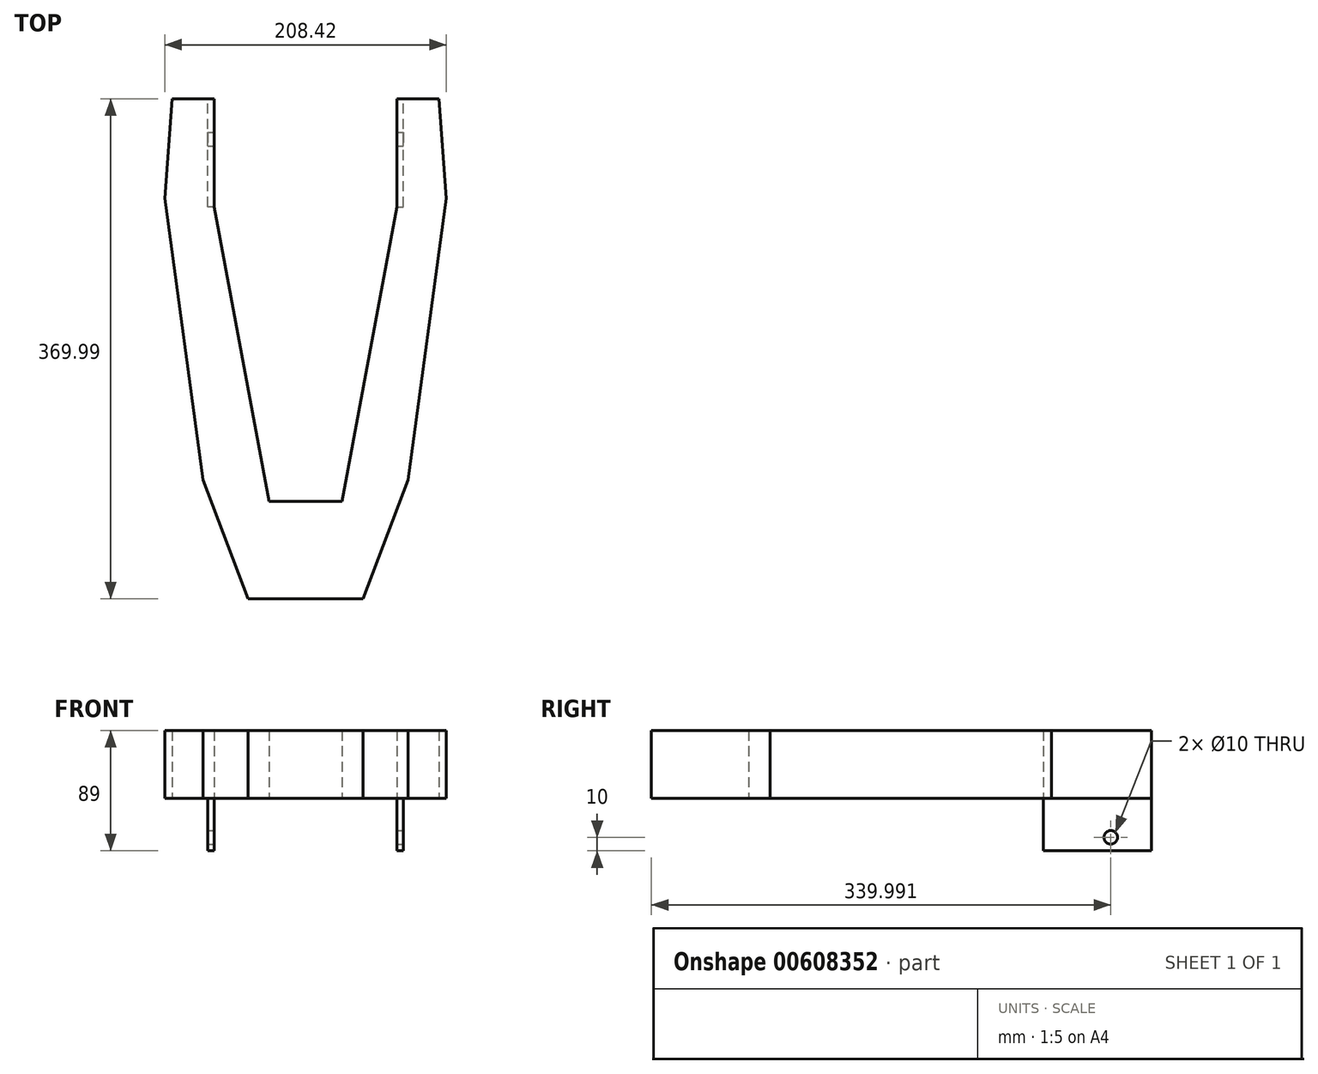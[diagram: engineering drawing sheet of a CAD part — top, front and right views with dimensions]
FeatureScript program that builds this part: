
annotation { "Feature Type Name" : "Feature", "Feature Type Description" : "" }
export const myFeature = defineFeature(function(context is Context, id is Id, definition is map)
    precondition{}
    {
        {
            var Q0;
            Q0=qCreatedBy(makeId("Top.planeOp"),FACE);
            var sketch = newSketch(context, id + "F0", { "sketchPlane" : qUnion([Q0])});
            skLineSegment(sketch, "E0", {"start": v(0, -141.26) * mm, "end": v(42.57, -141.26) * mm});
            skLineSegment(sketch, "E1", {"start": v(42.57, -141.26) * mm, "end": v(75.94, -53.33) * mm});
            skLineSegment(sketch, "E2", {"start": v(75.94, -53.33) * mm, "end": v(104.2, 154.89) * mm});
            skLineSegment(sketch, "E3", {"start": v(104.2, 154.89) * mm, "end": v(98.82, 228.73) * mm});
            skLineSegment(sketch, "E4", {"start": v(98.82, 228.73) * mm, "end": v(67.5, 228.73) * mm});
            skLineSegment(sketch, "E5", {"start": v(67.5, 228.73) * mm, "end": v(67.5, 148.73) * mm});
            skLineSegment(sketch, "E6", {"start": v(67.5, 148.73) * mm, "end": v(27, -69.27) * mm});
            skLineSegment(sketch, "E7", {"start": v(27, -69.27) * mm, "end": v(0, -69.27) * mm});
            skLineSegment(sketch, "E8.MirrorCS", {"start": v(-27, -69.27) * mm, "end": v(0, -69.27) * mm});
            skLineSegment(sketch, "E9.MirrorCS", {"start": v(-67.5, 148.73) * mm, "end": v(-27, -69.27) * mm});
            skLineSegment(sketch, "E10.MirrorCS", {"start": v(-67.5, 228.73) * mm, "end": v(-67.5, 148.73) * mm});
            skLineSegment(sketch, "E11.MirrorCS", {"start": v(-98.82, 228.73) * mm, "end": v(-67.5, 228.73) * mm});
            skLineSegment(sketch, "E12.MirrorCS", {"start": v(-104.2, 154.89) * mm, "end": v(-98.82, 228.73) * mm});
            skLineSegment(sketch, "E13.MirrorCS", {"start": v(-75.94, -53.33) * mm, "end": v(-104.2, 154.89) * mm});
            skLineSegment(sketch, "E14.MirrorCS", {"start": v(-42.57, -141.26) * mm, "end": v(-75.94, -53.33) * mm});
            skLineSegment(sketch, "E15.MirrorCS", {"start": v(0, -141.26) * mm, "end": v(-42.57, -141.26) * mm});
            skLineSegment(sketch, "E16", {"start": v(-67.5, 148.73) * mm, "end": v(-72.5, 148.73) * mm});
            skLineSegment(sketch, "E17", {"start": v(-72.5, 148.73) * mm, "end": v(-72.5, 228.73) * mm});
            skLineSegment(sketch, "E18.MirrorCS", {"start": v(67.5, 148.73) * mm, "end": v(72.5, 148.73) * mm});
            skLineSegment(sketch, "E19.MirrorCS", {"start": v(72.5, 148.73) * mm, "end": v(72.5, 228.73) * mm});
            skLineSegment(sketch, "E20", {"start": v(-67.5, 198.73) * mm, "end": v(67.5, 198.73) * mm, "construction": true});
            skLineSegment(sketch, "E21", {"start": v(-30.72, -49.27) * mm, "end": v(30.72, -49.27) * mm, "construction": true});
            skSolve(sketch);
        }
        {
            var Q0;
            Q0=makeQuery(id+"F0.imprint","IMPRINT",FACE,{"disambiguationData":[TD([[makeQuery(id+"F0.imprint","IMPRINT",EDGE,{"derivedFrom":sQuery(id+"F0.wireOp",EDGE,"E0")}),1.0]])]});
            var Q1;
            {var subQ0=sQuery(id+"F0.wireOp",EDGE,"E5");Q1=makeQuery(id+"F0.imprint","IMPRINT",FACE,{"disambiguationData":[TD([[makeQuery(id+"F0.imprint","IMPRINT",EDGE,{"derivedFrom":subQ0}),1.0]])]});}
            var Q2;
            {var subQ0=sQuery(id+"F0.wireOp",EDGE,"E10.MirrorCS");Q2=makeQuery(id+"F0.imprint","IMPRINT",FACE,{"disambiguationData":[TD([[makeQuery(id+"F0.imprint","IMPRINT",EDGE,{"derivedFrom":subQ0}),-1.0]])]});}
            extrude(context, id + "F1", {"entities" : qUnion([Q0, Q1, Q2]), "depth" : 50 * mm, "offsetDistance" : 25 * mm});
        }
        {
            var Q0;
            {var subQ0=sQuery(id+"F0.wireOp",EDGE,"E10.MirrorCS");Q0=makeQuery(id+"F0.imprint","IMPRINT",FACE,{"disambiguationData":[TD([[makeQuery(id+"F0.imprint","IMPRINT",EDGE,{"derivedFrom":subQ0}),-1.0]])]});}
            var Q1;
            {var subQ0=sQuery(id+"F0.wireOp",EDGE,"E5");Q1=makeQuery(id+"F0.imprint","IMPRINT",FACE,{"disambiguationData":[TD([[makeQuery(id+"F0.imprint","IMPRINT",EDGE,{"derivedFrom":subQ0}),1.0]])]});}
            extrude(context, id + "F2", {"entities" : qUnion([Q0, Q1]), "operationType" : NewBodyOperationType.ADD, "oppositeDirection" : true, "depth" : 39 * mm, "offsetDistance" : 25 * mm});
        }
        {
            var Q0;
            Q0=makeQuery(id+"F2.opExtrude","SWEPT_FACE",FACE,{"disambiguationData":[OSD([sQuery(id+"F0.wireOp",EDGE,"E19.MirrorCS")])]});
            var sketch = newSketch(context, id + "F3", { "sketchPlane" : qUnion([Q0])});
            skCircle(sketch, "E22", {"center": v(198.73, -29) * mm, "radius": 5 * mm});
            skSolve(sketch);
        }
        {
            var Q0;
            Q0=sQuery(id+"F3.wireOp",VERTEX,"E22.center");
            var Q1;
            Q1=makeQuery(id+"F1.opExtrude","SWEPT_BODY",BODY,{"disambiguationData":[OSD([sQuery(id+"F0.wireOp",EDGE,"E0"),sQuery(id+"F0.wireOp",EDGE,"E1"),sQuery(id+"F0.wireOp",EDGE,"E2"),sQuery(id+"F0.wireOp",EDGE,"E3"),sQuery(id+"F0.wireOp",EDGE,"E4"),sQuery(id+"F0.wireOp",EDGE,"E5"),sQuery(id+"F0.wireOp",EDGE,"E6"),sQuery(id+"F0.wireOp",EDGE,"E7"),sQuery(id+"F0.wireOp",EDGE,"E8.MirrorCS"),sQuery(id+"F0.wireOp",EDGE,"E9.MirrorCS"),sQuery(id+"F0.wireOp",EDGE,"E10.MirrorCS"),sQuery(id+"F0.wireOp",EDGE,"E11.MirrorCS"),sQuery(id+"F0.wireOp",EDGE,"E12.MirrorCS"),sQuery(id+"F0.wireOp",EDGE,"E13.MirrorCS"),sQuery(id+"F0.wireOp",EDGE,"E14.MirrorCS"),sQuery(id+"F0.wireOp",EDGE,"E15.MirrorCS")])]});
            hole(context, id + "F4", {"style" : HoleStyle.SIMPLE, "endStyle" : HoleEndStyle.THROUGH, "holeDiameter" : 10 * mm, "majorDiameter" : 5 * mm, "isTappedThrough" : true, "tappedDepth" : 12 * mm, "tapClearance" : 3, "locations" : qUnion([Q0]), "scope" : qUnion([Q1])});
        }
    });
